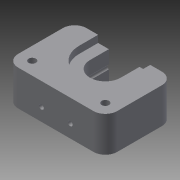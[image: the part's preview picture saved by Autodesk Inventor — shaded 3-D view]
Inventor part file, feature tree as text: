
AUTODESK INVENTOR PART (.ipt)
format: ipt  version: 2013 (Build 170138000, 138)  size: 142,336 bytes
history: native  units: mm
features: extrude x5, sketch x5, fillet x1
ambient origin geometry x8: Origin, YZ Plane, XZ Plane, XY Plane, X Axis, Y Axis, Z Axis, Center Point
bodies: Solid1 (feature_tree)
feature tree (11):
  extrude  "Extrusion1"  Depth=42.0mm
  fillet  "Fillet1"  Radius=29.0mm
  extrude  "Extrusion2"  Depth=5.0mm
  extrude  "Extrusion3"  Depth=3.0mm TaperAngle=0.0deg
  extrude  "Extrusion4"  Depth=3.0mm TaperAngle=0.0deg
  extrude  "Extrusion5"  Depth=12.25mm
  sketch  "Sketch1"  dims[d0=21.0mm d1=42.0mm d2=29.0mm]
  sketch  "Sketch2"  dims[d3=15.0mm d4=0.0mm d5=5.0mm]
  sketch  "Sketch3"  dims[d6=11.05mm d8=3.0mm d9=0.0mm]
  sketch  "Sketch4"  dims[d10=13.0mm d12=3.0mm d13=0.0mm]
  sketch  "Sketch5"  dims[d14=5.5mm d15=12.25mm d16=2.0mm d17=3.0mm d18=0.0mm d19=31.0mm d20=3.1mm d21=3.0mm d22=0.0mm]
